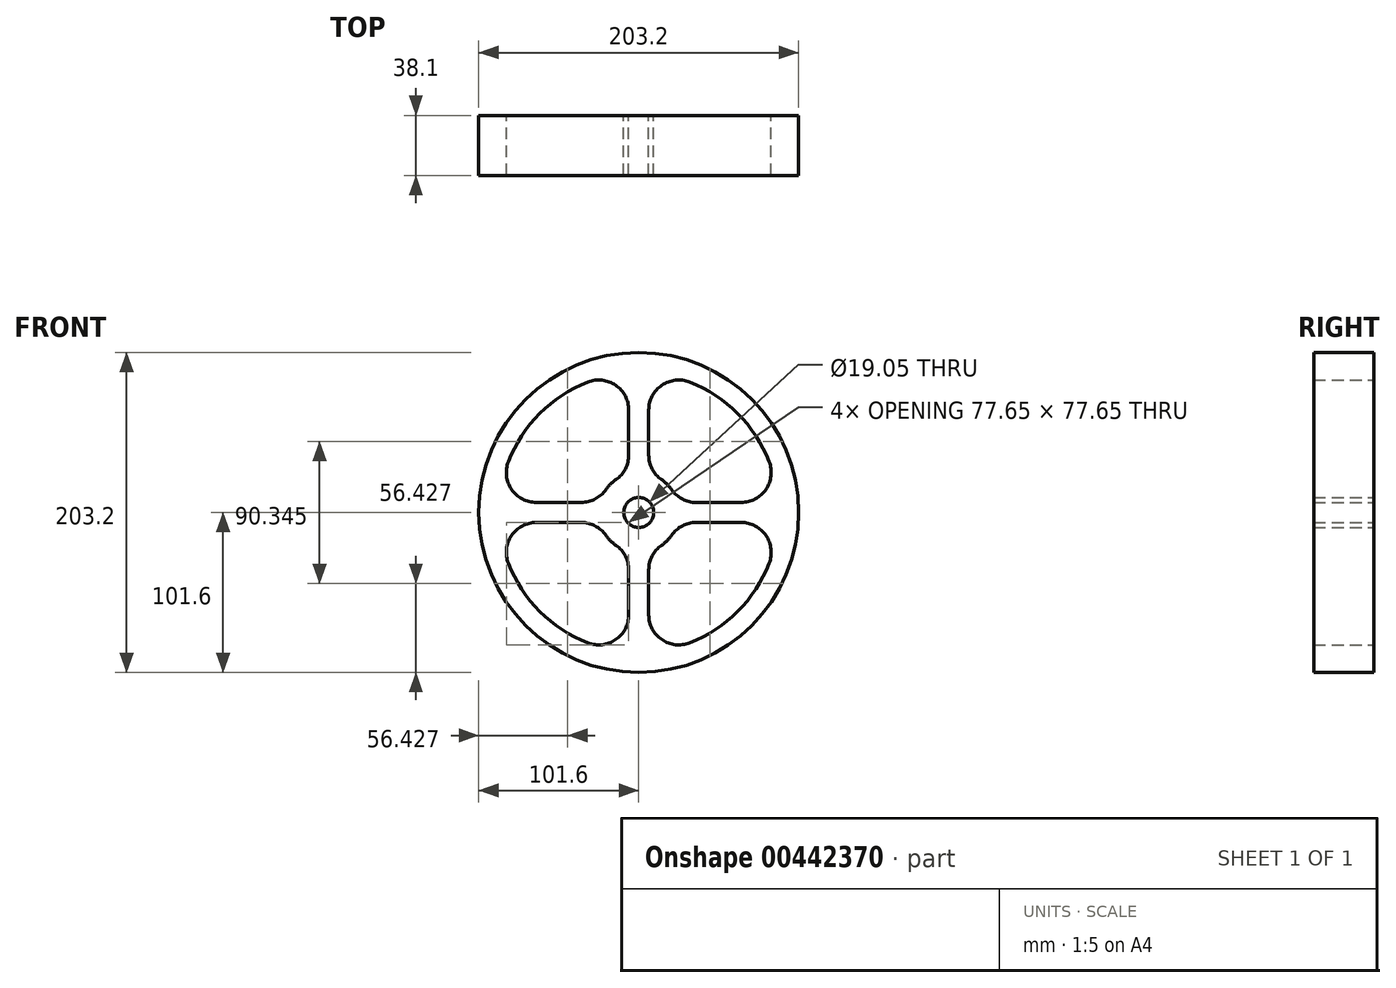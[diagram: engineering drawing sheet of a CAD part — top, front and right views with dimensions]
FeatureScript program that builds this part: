
annotation { "Feature Type Name" : "Feature", "Feature Type Description" : "" }
export const myFeature = defineFeature(function(context is Context, id is Id, definition is map)
    precondition{}
    {
        {
            var Q0;
            Q0=qCreatedBy(makeId("Front.planeOp"),FACE);
            var sketch = newSketch(context, id + "F0", { "sketchPlane" : qUnion([Q0])});
            skCircle(sketch, "E0", {"center": v(0, 0) * mm, "radius": 101.6 * mm});
            skArc(sketch, "E1", {"start": v(-82.81, -32.33) * mm, "mid": v(-62.86, -62.86) * mm, "end": v(-32.33, -82.81) * mm});
            skArc(sketch, "E2", {"start": v(-20.84, -14.51) * mm, "mid": v(-17.96, -17.96) * mm, "end": v(-14.51, -20.84) * mm});
            skLineSegment(sketch, "E3", {"start": v(6.35, 65.07) * mm, "end": v(6.35, 36.48) * mm});
            skArc(sketch, "E4", {"start": v(-82.81, 32.33) * mm, "mid": v(-80.8, 14.65) * mm, "end": v(-65.07, 6.35) * mm});
            skArc(sketch, "E5", {"start": v(-6.35, 65.07) * mm, "mid": v(-14.65, 80.8) * mm, "end": v(-32.33, 82.81) * mm});
            skLineSegment(sketch, "E6.trimOffspring", {"start": v(-65.07, 6.35) * mm, "end": v(-36.48, 6.35) * mm});
            skArc(sketch, "E7.trimOffspring", {"start": v(-32.33, 82.81) * mm, "mid": v(-62.86, 62.86) * mm, "end": v(-82.81, 32.33) * mm});
            skLineSegment(sketch, "E8.trimOffspring", {"start": v(-6.35, 65.07) * mm, "end": v(-6.35, 36.48) * mm});
            skPoint(sketch, "E9.start.orphan", {"position": v(0, 122.07) * mm});
            skLineSegment(sketch, "E10.trimOffspring", {"start": v(36.48, 6.35) * mm, "end": v(65.07, 6.35) * mm});
            skLineSegment(sketch, "E11.trimOffspring", {"start": v(36.48, -6.35) * mm, "end": v(65.07, -6.35) * mm});
            skLineSegment(sketch, "E12.trimOffspring", {"start": v(-6.35, -36.48) * mm, "end": v(-6.35, -65.07) * mm});
            skLineSegment(sketch, "E13.trimOffspring", {"start": v(6.35, -36.48) * mm, "end": v(6.35, -65.07) * mm});
            skArc(sketch, "E14", {"start": v(-36.48, 6.35) * mm, "mid": v(-27.66, 8.51) * mm, "end": v(-20.84, 14.51) * mm});
            skArc(sketch, "E15", {"start": v(-14.51, 20.84) * mm, "mid": v(-8.51, 27.66) * mm, "end": v(-6.35, 36.48) * mm});
            skArc(sketch, "E16.trimOffspring", {"start": v(-14.51, 20.84) * mm, "mid": v(-17.96, 17.96) * mm, "end": v(-20.84, 14.51) * mm});
            skArc(sketch, "E17", {"start": v(-65.07, -6.35) * mm, "mid": v(-80.8, -14.65) * mm, "end": v(-82.81, -32.33) * mm});
            skArc(sketch, "E18", {"start": v(-32.33, -82.81) * mm, "mid": v(-14.65, -80.8) * mm, "end": v(-6.35, -65.07) * mm});
            skArc(sketch, "E19", {"start": v(-20.84, -14.51) * mm, "mid": v(-27.66, -8.51) * mm, "end": v(-36.48, -6.35) * mm});
            skArc(sketch, "E20.trimOffspring", {"start": v(-6.35, -36.48) * mm, "mid": v(-8.51, -27.66) * mm, "end": v(-14.51, -20.84) * mm});
            skLineSegment(sketch, "E21.trimOffspring", {"start": v(-65.07, -6.35) * mm, "end": v(-36.48, -6.35) * mm});
            skArc(sketch, "E22.trimOffspring", {"start": v(32.33, -82.81) * mm, "mid": v(62.86, -62.86) * mm, "end": v(82.81, -32.33) * mm});
            skArc(sketch, "E23", {"start": v(6.35, -65.07) * mm, "mid": v(14.65, -80.8) * mm, "end": v(32.33, -82.81) * mm});
            skArc(sketch, "E24", {"start": v(82.81, -32.33) * mm, "mid": v(80.8, -14.65) * mm, "end": v(65.07, -6.35) * mm});
            skArc(sketch, "E25.trimOffspring", {"start": v(14.51, -20.84) * mm, "mid": v(8.51, -27.66) * mm, "end": v(6.35, -36.48) * mm});
            skArc(sketch, "E26.trimOffspring", {"start": v(36.48, -6.35) * mm, "mid": v(27.66, -8.51) * mm, "end": v(20.84, -14.51) * mm});
            skArc(sketch, "E27", {"start": v(32.33, 82.81) * mm, "mid": v(14.65, 80.8) * mm, "end": v(6.35, 65.07) * mm});
            skArc(sketch, "E28", {"start": v(65.07, 6.35) * mm, "mid": v(80.8, 14.65) * mm, "end": v(82.81, 32.33) * mm});
            skArc(sketch, "E29", {"start": v(20.84, 14.51) * mm, "mid": v(27.66, 8.51) * mm, "end": v(36.48, 6.35) * mm});
            skArc(sketch, "E30", {"start": v(6.35, 36.48) * mm, "mid": v(8.51, 27.66) * mm, "end": v(14.51, 20.84) * mm});
            skArc(sketch, "E31.trimOffspring", {"start": v(20.84, 14.51) * mm, "mid": v(17.96, 17.96) * mm, "end": v(14.51, 20.84) * mm});
            skArc(sketch, "E32.trimOffspring", {"start": v(14.51, -20.84) * mm, "mid": v(17.96, -17.96) * mm, "end": v(20.84, -14.51) * mm});
            skPoint(sketch, "E33.trimOffspring.end.orphan", {"position": v(137.38, 0) * mm});
            skArc(sketch, "E34.trimOffspring", {"start": v(82.81, 32.33) * mm, "mid": v(62.86, 62.86) * mm, "end": v(32.33, 82.81) * mm});
            skPoint(sketch, "E35.start.orphan", {"position": v(-126.93, 0) * mm});
            skPoint(sketch, "E36.trimOffspring.end.orphan", {"position": v(0, -123.2) * mm});
            skCircle(sketch, "E37", {"center": v(0, 0) * mm, "radius": 9.53 * mm});
            skSolve(sketch);
        }
        {
            var Q0;
            Q0 = qSketchRegion(id + "F0", true);
            extrude(context, id + "F1", {"entities" : qUnion([Q0]), "depth" : 38.1 * mm});
        }
    });
